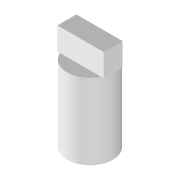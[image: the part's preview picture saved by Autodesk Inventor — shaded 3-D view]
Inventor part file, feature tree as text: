
AUTODESK INVENTOR PART (.ipt)
format: ipt  version: 2022 (Build 260153000, 153)  size: 87,040 bytes
history: native  units: mm
features: extrude x2, sketch x2
ambient origin geometry x8: Origin, YZ Plane, XZ Plane, XY Plane, X Axis, Y Axis, Z Axis, Center Point
bodies: Volumenkörper1 (feature_tree)
feature tree (4):
  extrude  "Extrusion1"  Depth=10.0mm TaperAngle=0.0deg
  extrude  "Extrusion2"  Depth=2.5mm
  sketch  "Skizze1"  dims[d0=6.0mm d1=10.0mm d2=0.0mm]
  sketch  "Skizze2"  dims[d3=6.1mm d4=2.5mm d5=3.0mm d6=0.0mm]
